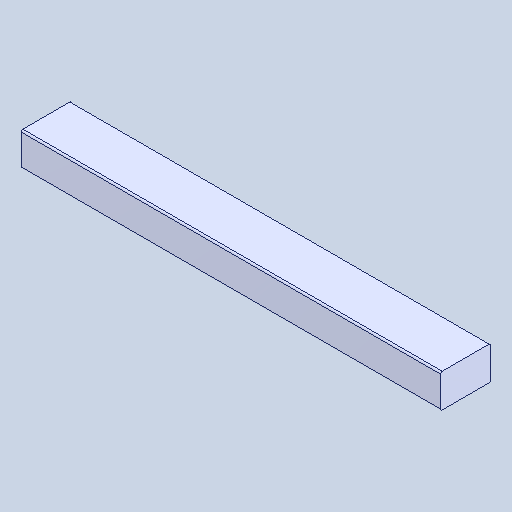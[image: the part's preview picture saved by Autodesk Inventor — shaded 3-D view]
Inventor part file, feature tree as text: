
AUTODESK INVENTOR PART (.ipt)
format: ipt  version: 2024.1 (Build 281209000, 209)  size: 84,480 bytes
history: native  units: in
note: dims shown in document units (in); Inventor stores cm internally (conversion verified against a paired STEP export)
features: fillet x1
ambient origin geometry x8: Origin, YZ Plane, XZ Plane, XY Plane, X Axis, Y Axis, Z Axis, Center Point
bodies: Solid1 (feature_tree)
feature tree (1):
  fillet  "Fillet1"  [1 undecoded]
note: 1 required parameter value undecoded (feature->parameter linkage not recoverable at this tier; creation-order binding heuristic only, values carry confidence <= 0.55)
